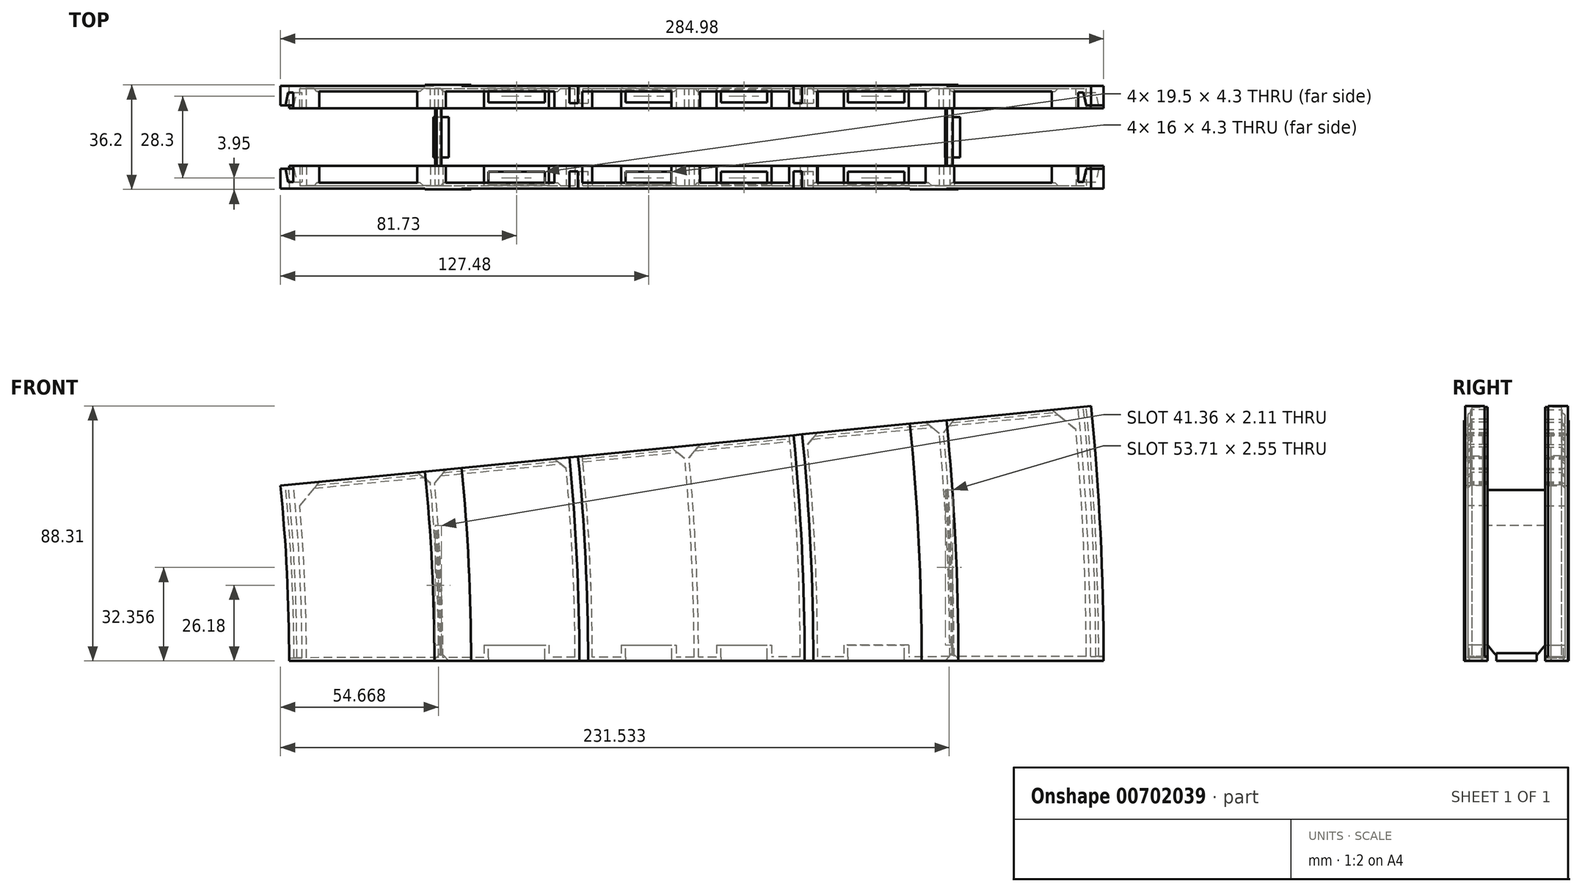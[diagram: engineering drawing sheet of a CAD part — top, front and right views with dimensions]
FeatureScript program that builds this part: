
annotation { "Feature Type Name" : "Feature", "Feature Type Description" : "" }
export const myFeature = defineFeature(function(context is Context, id is Id, definition is map)
    precondition{}
    {
        {
            var Q0;
            Q0=qCreatedBy(makeId("Top.planeOp"),FACE);
            var sketch = newSketch(context, id + "F0", { "sketchPlane" : qUnion([Q0])});
            skLineSegment(sketch, "E0", {"start": v(0, 7.8) * mm, "end": v(37.5, 7.8) * mm});
            skLineSegment(sketch, "E1", {"start": v(156, 0) * mm, "end": v(0, 0) * mm});
            skLineSegment(sketch, "E2", {"start": v(0, 0) * mm, "end": v(0, 7.8) * mm});
            skLineSegment(sketch, "E3.top", {"start": v(37.5, 1.8) * mm, "end": v(40.5, 1.8) * mm});
            skLineSegment(sketch, "E3.left", {"start": v(37.5, 7.8) * mm, "end": v(37.5, 1.8) * mm});
            skLineSegment(sketch, "E3.right", {"start": v(40.5, 7.8) * mm, "end": v(40.5, 1.8) * mm});
            skLineSegment(sketch, "E4.top", {"start": v(115.5, 1.8) * mm, "end": v(118.5, 1.8) * mm});
            skLineSegment(sketch, "E4.left", {"start": v(115.5, 7.8) * mm, "end": v(115.5, 1.8) * mm});
            skLineSegment(sketch, "E4.right", {"start": v(118.5, 7.8) * mm, "end": v(118.5, 1.8) * mm});
            skLineSegment(sketch, "E5.trimOffspring", {"start": v(40.5, 7.8) * mm, "end": v(115.5, 7.8) * mm});
            skLineSegment(sketch, "E6.trimOffspring", {"start": v(118.5, 7.8) * mm, "end": v(156, 7.8) * mm});
            skLineSegment(sketch, "E7.bottom", {"start": v(6, 6.3) * mm, "end": v(25.5, 6.3) * mm});
            skLineSegment(sketch, "E7.top", {"start": v(6, 2) * mm, "end": v(25.5, 2) * mm});
            skLineSegment(sketch, "E7.left", {"start": v(6, 6.3) * mm, "end": v(6, 2) * mm});
            skLineSegment(sketch, "E7.right", {"start": v(25.5, 6.3) * mm, "end": v(25.5, 2) * mm});
            skLineSegment(sketch, "E8.bottom", {"start": v(53.5, 6.3) * mm, "end": v(69.5, 6.3) * mm});
            skLineSegment(sketch, "E8.top", {"start": v(53.5, 2) * mm, "end": v(69.5, 2) * mm});
            skLineSegment(sketch, "E8.left", {"start": v(53.5, 6.3) * mm, "end": v(53.5, 2) * mm});
            skLineSegment(sketch, "E8.right", {"start": v(69.5, 6.3) * mm, "end": v(69.5, 2) * mm});
            skLineSegment(sketch, "E9.bottom", {"start": v(86.5, 6.3) * mm, "end": v(102.5, 6.3) * mm});
            skLineSegment(sketch, "E9.top", {"start": v(86.5, 2) * mm, "end": v(102.5, 2) * mm});
            skLineSegment(sketch, "E9.left", {"start": v(86.5, 6.3) * mm, "end": v(86.5, 2) * mm});
            skLineSegment(sketch, "E9.right", {"start": v(102.5, 6.3) * mm, "end": v(102.5, 2) * mm});
            skLineSegment(sketch, "E10.bottom", {"start": v(130.5, 6.3) * mm, "end": v(150, 6.3) * mm});
            skLineSegment(sketch, "E10.top", {"start": v(130.5, 2) * mm, "end": v(150, 2) * mm});
            skLineSegment(sketch, "E10.left", {"start": v(130.5, 6.3) * mm, "end": v(130.5, 2) * mm});
            skLineSegment(sketch, "E10.right", {"start": v(150, 6.3) * mm, "end": v(150, 2) * mm});
            skLineSegment(sketch, "E11", {"start": v(-682, 44.9) * mm, "end": v(-682, -42.13) * mm});
            skLineSegment(sketch, "E12", {"start": v(156, 7.8) * mm, "end": v(219, 7.8) * mm});
            skLineSegment(sketch, "E13", {"start": v(219, 7.8) * mm, "end": v(219, 0) * mm});
            skLineSegment(sketch, "E14", {"start": v(219, 0) * mm, "end": v(156, 0) * mm});
            skLineSegment(sketch, "E15", {"start": v(0, 0) * mm, "end": v(-63, 0) * mm});
            skLineSegment(sketch, "E16", {"start": v(-63, 0) * mm, "end": v(-63, 7.8) * mm});
            skLineSegment(sketch, "E17", {"start": v(-63, 7.8) * mm, "end": v(0, 7.8) * mm});
            skLineSegment(sketch, "E18", {"start": v(156, 7.8) * mm, "end": v(156, 0) * mm});
            skSolve(sketch);
        }
        {
            var Q0;
            Q0=makeQuery(id+"F0.imprint","IMPRINT",FACE,{"disambiguationData":[TD([[makeQuery(id+"F0.imprint","IMPRINT",EDGE,{"derivedFrom":sQuery(id+"F0.wireOp",EDGE,"E0")}),-1.0]])]});
            var Q1;
            Q1=makeQuery(id+"F0.imprint","IMPRINT",FACE,{"disambiguationData":[TD([[makeQuery(id+"F0.imprint","IMPRINT",EDGE,{"derivedFrom":sQuery(id+"F0.wireOp",EDGE,"E2")}),1.0]])]});
            var Q2;
            Q2=makeQuery(id+"F0.imprint","IMPRINT",FACE,{"disambiguationData":[TD([[makeQuery(id+"F0.imprint","IMPRINT",EDGE,{"derivedFrom":sQuery(id+"F0.wireOp",EDGE,"E12")}),-1.0]])]});
            var Q3;
            Q3=sQuery(id+"F0.wireOp",EDGE,"E11");
            revolve(context, id + "F1", {"entities" : qUnion([Q0, Q1, Q2]), "axis" : qUnion([Q3]), "revolveType" : RevolveType.ONE_DIRECTION, "angle" : .1 * degree});
        }
        {
            var Q0;
            Q0=makeQuery(id+"F1.opRevolve","CAP_FACE",FACE,{"disambiguationData":[OSD([sQuery(id+"F0.wireOp",EDGE,"E0"),sQuery(id+"F0.wireOp",EDGE,"E1"),sQuery(id+"F0.wireOp",EDGE,"E3.top"),sQuery(id+"F0.wireOp",EDGE,"E3.left"),sQuery(id+"F0.wireOp",EDGE,"E3.right"),sQuery(id+"F0.wireOp",EDGE,"E4.top"),sQuery(id+"F0.wireOp",EDGE,"E4.left"),sQuery(id+"F0.wireOp",EDGE,"E4.right"),sQuery(id+"F0.wireOp",EDGE,"E5.trimOffspring"),sQuery(id+"F0.wireOp",EDGE,"E6.trimOffspring"),sQuery(id+"F0.wireOp",EDGE,"E7.bottom"),sQuery(id+"F0.wireOp",EDGE,"E7.top"),sQuery(id+"F0.wireOp",EDGE,"E7.left"),sQuery(id+"F0.wireOp",EDGE,"E7.right"),sQuery(id+"F0.wireOp",EDGE,"E8.bottom"),sQuery(id+"F0.wireOp",EDGE,"E8.top"),sQuery(id+"F0.wireOp",EDGE,"E8.left"),sQuery(id+"F0.wireOp",EDGE,"E8.right"),sQuery(id+"F0.wireOp",EDGE,"E9.bottom"),sQuery(id+"F0.wireOp",EDGE,"E9.top"),sQuery(id+"F0.wireOp",EDGE,"E9.left"),sQuery(id+"F0.wireOp",EDGE,"E9.right"),sQuery(id+"F0.wireOp",EDGE,"E10.bottom"),sQuery(id+"F0.wireOp",EDGE,"E10.top"),sQuery(id+"F0.wireOp",EDGE,"E10.left"),sQuery(id+"F0.wireOp",EDGE,"E10.right"),sQuery(id+"F0.wireOp",EDGE,"E12"),sQuery(id+"F0.wireOp",EDGE,"E13"),sQuery(id+"F0.wireOp",EDGE,"E14"),sQuery(id+"F0.wireOp",EDGE,"E15"),sQuery(id+"F0.wireOp",EDGE,"E16"),sQuery(id+"F0.wireOp",EDGE,"E17")])],"isStart":true});
            var sketch = newSketch(context, id + "F2", { "sketchPlane" : qUnion([Q0])});
            skLineSegment(sketch, "E19", {"start": v(219, -7.8) * mm, "end": v(219, -1) * mm});
            skLineSegment(sketch, "E20", {"start": v(219, -1) * mm, "end": v(217.3, -1) * mm});
            skLineSegment(sketch, "E21", {"start": v(217.3, -1) * mm, "end": v(216.3, -5.5) * mm});
            skLineSegment(sketch, "E22", {"start": v(216.3, -5.5) * mm, "end": v(214.5, -5.5) * mm});
            skLineSegment(sketch, "E23", {"start": v(214.5, -5.5) * mm, "end": v(214.5, 0) * mm});
            skLineSegment(sketch, "E24", {"start": v(214.5, 0) * mm, "end": v(213, 0) * mm});
            skLineSegment(sketch, "E25", {"start": v(213, 0) * mm, "end": v(213, -6.8) * mm});
            skLineSegment(sketch, "E26", {"start": v(213, -6.8) * mm, "end": v(167.25, -6.8) * mm});
            skLineSegment(sketch, "E27", {"start": v(167.25, -6.8) * mm, "end": v(167.25, 0) * mm});
            skLineSegment(sketch, "E28", {"start": v(167.25, 0) * mm, "end": v(165.75, 0) * mm});
            skLineSegment(sketch, "E29", {"start": v(165.75, 0) * mm, "end": v(165.75, -6.8) * mm});
            skLineSegment(sketch, "E30", {"start": v(165.75, -6.8) * mm, "end": v(120, -6.8) * mm});
            skLineSegment(sketch, "E31", {"start": v(120, -6.8) * mm, "end": v(120, 0) * mm});
            skLineSegment(sketch, "E32", {"start": v(120, 0) * mm, "end": v(114, 0) * mm});
            skLineSegment(sketch, "E33", {"start": v(114, 0) * mm, "end": v(114, -6.8) * mm});
            skLineSegment(sketch, "E34", {"start": v(114, -6.8) * mm, "end": v(78.75, -6.8) * mm});
            skLineSegment(sketch, "E35", {"start": v(78.75, -6.8) * mm, "end": v(78.75, 0) * mm});
            skLineSegment(sketch, "E36", {"start": v(78.75, 0) * mm, "end": v(77.25, 0) * mm});
            skLineSegment(sketch, "E37", {"start": v(77.25, 0) * mm, "end": v(77.25, -6.8) * mm});
            skLineSegment(sketch, "E38", {"start": v(77.25, -6.8) * mm, "end": v(42, -6.8) * mm});
            skLineSegment(sketch, "E39", {"start": v(42, -6.8) * mm, "end": v(42, 0) * mm});
            skLineSegment(sketch, "E40", {"start": v(42, 0) * mm, "end": v(36, 0) * mm});
            skLineSegment(sketch, "E41", {"start": v(36, 0) * mm, "end": v(36, -6.8) * mm});
            skLineSegment(sketch, "E42", {"start": v(36, -6.8) * mm, "end": v(-9.75, -6.8) * mm});
            skLineSegment(sketch, "E43", {"start": v(-9.75, -6.8) * mm, "end": v(-9.75, 0) * mm});
            skLineSegment(sketch, "E44", {"start": v(-9.75, 0) * mm, "end": v(-11.25, 0) * mm});
            skLineSegment(sketch, "E45", {"start": v(-11.25, 0) * mm, "end": v(-11.25, -6.8) * mm});
            skLineSegment(sketch, "E46", {"start": v(-11.25, -6.8) * mm, "end": v(-57, -6.8) * mm});
            skLineSegment(sketch, "E47", {"start": v(-57, -6.8) * mm, "end": v(-57, 0) * mm});
            skLineSegment(sketch, "E48", {"start": v(-57, 0) * mm, "end": v(-58.5, 0) * mm});
            skLineSegment(sketch, "E49", {"start": v(-58.5, 0) * mm, "end": v(-58.5, -5.5) * mm});
            skLineSegment(sketch, "E50", {"start": v(-58.5, -5.5) * mm, "end": v(-60.3, -5.5) * mm});
            skLineSegment(sketch, "E51", {"start": v(-60.3, -5.5) * mm, "end": v(-61.3, -1) * mm});
            skLineSegment(sketch, "E52", {"start": v(-61.3, -1) * mm, "end": v(-63, -1) * mm});
            skLineSegment(sketch, "E53", {"start": v(-63, -1) * mm, "end": v(-63, -7.8) * mm});
            skLineSegment(sketch, "E54", {"start": v(-63, -7.8) * mm, "end": v(37.5, -7.8) * mm});
            skLineSegment(sketch, "E55", {"start": v(37.5, -7.8) * mm, "end": v(37.5, -1.8) * mm});
            skLineSegment(sketch, "E56", {"start": v(37.5, -1.8) * mm, "end": v(40.5, -1.8) * mm});
            skLineSegment(sketch, "E57", {"start": v(40.5, -1.8) * mm, "end": v(40.5, -7.8) * mm});
            skLineSegment(sketch, "E58", {"start": v(40.5, -7.8) * mm, "end": v(115.5, -7.8) * mm});
            skLineSegment(sketch, "E59", {"start": v(115.5, -7.8) * mm, "end": v(115.5, -1.8) * mm});
            skLineSegment(sketch, "E60", {"start": v(115.5, -1.8) * mm, "end": v(118.5, -1.8) * mm});
            skLineSegment(sketch, "E61", {"start": v(118.5, -1.8) * mm, "end": v(118.5, -7.8) * mm});
            skLineSegment(sketch, "E62", {"start": v(118.5, -7.8) * mm, "end": v(219, -7.8) * mm});
            skLineSegment(sketch, "E63", {"start": v(-682, -85.53) * mm, "end": v(-682, 67.73) * mm});
            skSolve(sketch);
        }
        {
            var Q0;
            Q0=makeQuery(id+"F2.imprint","IMPRINT",FACE,{"disambiguationData":[TD([[makeQuery(id+"F2.imprint","IMPRINT",EDGE,{"derivedFrom":sQuery(id+"F2.wireOp",EDGE,"E19")}),1.0]])]});
            var Q1;
            Q1=sQuery(id+"F2.wireOp",EDGE,"E63");
            revolve(context, id + "F3", {"operationType" : NewBodyOperationType.ADD, "entities" : qUnion([Q0]), "axis" : qUnion([Q1]), "revolveType" : RevolveType.ONE_DIRECTION, "angle" : 5.62 * degree});
        }
        {
            var Q0;
            Q0=qCreatedBy(makeId("Top.planeOp"),FACE);
            var sketch = newSketch(context, id + "F4", { "sketchPlane" : qUnion([Q0])});
            skLineSegment(sketch, "E64.bottom", {"start": v(4.5, 0) * mm, "end": v(27, 0) * mm});
            skLineSegment(sketch, "E64.top", {"start": v(4.5, 7.8) * mm, "end": v(27, 7.8) * mm});
            skLineSegment(sketch, "E64.left", {"start": v(4.5, 0) * mm, "end": v(4.5, 7.8) * mm});
            skLineSegment(sketch, "E64.right", {"start": v(27, 0) * mm, "end": v(27, 7.8) * mm});
            skLineSegment(sketch, "E65.bottom", {"start": v(6, 2) * mm, "end": v(25.5, 2) * mm});
            skLineSegment(sketch, "E65.top", {"start": v(6, 6.3) * mm, "end": v(25.5, 6.3) * mm});
            skLineSegment(sketch, "E65.left", {"start": v(6, 2) * mm, "end": v(6, 6.3) * mm});
            skLineSegment(sketch, "E65.right", {"start": v(25.5, 2) * mm, "end": v(25.5, 6.3) * mm});
            skLineSegment(sketch, "E66.bottom", {"start": v(52, 0) * mm, "end": v(71, 0) * mm});
            skLineSegment(sketch, "E66.top", {"start": v(52, 7.8) * mm, "end": v(71, 7.8) * mm});
            skLineSegment(sketch, "E66.left", {"start": v(52, 0) * mm, "end": v(52, 7.8) * mm});
            skLineSegment(sketch, "E66.right", {"start": v(71, 0) * mm, "end": v(71, 7.8) * mm});
            skLineSegment(sketch, "E67.bottom", {"start": v(53.5, 2) * mm, "end": v(69.5, 2) * mm});
            skLineSegment(sketch, "E67.top", {"start": v(53.5, 6.3) * mm, "end": v(69.5, 6.3) * mm});
            skLineSegment(sketch, "E67.left", {"start": v(53.5, 2) * mm, "end": v(53.5, 6.3) * mm});
            skLineSegment(sketch, "E67.right", {"start": v(69.5, 2) * mm, "end": v(69.5, 6.3) * mm});
            skLineSegment(sketch, "E68.bottom", {"start": v(85, 0) * mm, "end": v(104, 0) * mm});
            skLineSegment(sketch, "E68.top", {"start": v(85, 7.8) * mm, "end": v(104, 7.8) * mm});
            skLineSegment(sketch, "E68.left", {"start": v(85, 0) * mm, "end": v(85, 7.8) * mm});
            skLineSegment(sketch, "E68.right", {"start": v(104, 0) * mm, "end": v(104, 7.8) * mm});
            skLineSegment(sketch, "E69.bottom", {"start": v(86.5, 2) * mm, "end": v(102.5, 2) * mm});
            skLineSegment(sketch, "E69.top", {"start": v(86.5, 6.3) * mm, "end": v(102.5, 6.3) * mm});
            skLineSegment(sketch, "E69.left", {"start": v(86.5, 2) * mm, "end": v(86.5, 6.3) * mm});
            skLineSegment(sketch, "E69.right", {"start": v(102.5, 2) * mm, "end": v(102.5, 6.3) * mm});
            skLineSegment(sketch, "E70.top", {"start": v(129, 7.8) * mm, "end": v(151.5, 7.8) * mm});
            skLineSegment(sketch, "E70.left", {"start": v(129, 0) * mm, "end": v(129, 7.8) * mm});
            skLineSegment(sketch, "E70.right", {"start": v(151.5, 0) * mm, "end": v(151.5, 7.8) * mm});
            skLineSegment(sketch, "E71.top", {"start": v(130.5, 6.3) * mm, "end": v(150, 6.3) * mm});
            skLineSegment(sketch, "E71.left", {"start": v(130.5, 2) * mm, "end": v(130.5, 6.3) * mm});
            skLineSegment(sketch, "E71.right", {"start": v(150, 2) * mm, "end": v(150, 6.3) * mm});
            skLineSegment(sketch, "E72", {"start": v(150, 2) * mm, "end": v(130.5, 2) * mm});
            skLineSegment(sketch, "E73", {"start": v(151.5, 0) * mm, "end": v(129, 0) * mm});
            skSolve(sketch);
        }
        {
            var Q0;
            Q0=makeQuery(id+"F4.imprint","IMPRINT",FACE,{"disambiguationData":[TD([[makeQuery(id+"F4.imprint","IMPRINT",EDGE,{"derivedFrom":sQuery(id+"F4.wireOp",EDGE,"E70.top")}),-1.0]])]});
            var Q1;
            Q1=makeQuery(id+"F4.imprint","IMPRINT",FACE,{"disambiguationData":[TD([[makeQuery(id+"F4.imprint","IMPRINT",EDGE,{"derivedFrom":sQuery(id+"F4.wireOp",EDGE,"E68.bottom")}),1.0]])]});
            var Q2;
            Q2=makeQuery(id+"F4.imprint","IMPRINT",FACE,{"disambiguationData":[TD([[makeQuery(id+"F4.imprint","IMPRINT",EDGE,{"derivedFrom":sQuery(id+"F4.wireOp",EDGE,"E66.bottom")}),1.0]])]});
            var Q3;
            Q3=makeQuery(id+"F4.imprint","IMPRINT",FACE,{"disambiguationData":[TD([[makeQuery(id+"F4.imprint","IMPRINT",EDGE,{"derivedFrom":sQuery(id+"F4.wireOp",EDGE,"E64.bottom")}),1.0]])]});
            extrude(context, id + "F5", {"entities" : qUnion([Q0, Q1, Q2, Q3]), "operationType" : NewBodyOperationType.ADD, "depth" : 5.5 * mm, "offsetDistance" : 25 * mm});
        }
        {
            var Q0;
            Q0=makeQuery(id+"FsCbM9j6MyeHqur_1.boolean.opBoolean","MERGE",FACE,{"derivedFrom":[makeQuery(id+"F3.opRevolve","CAP_FACE",FACE,{"disambiguationData":[OSD([sQuery(id+"F2.wireOp",EDGE,"E19"),sQuery(id+"F2.wireOp",EDGE,"E20"),sQuery(id+"F2.wireOp",EDGE,"E21"),sQuery(id+"F2.wireOp",EDGE,"E22"),sQuery(id+"F2.wireOp",EDGE,"E23"),sQuery(id+"F2.wireOp",EDGE,"E24"),sQuery(id+"F2.wireOp",EDGE,"E25"),sQuery(id+"F2.wireOp",EDGE,"E26"),sQuery(id+"F2.wireOp",EDGE,"E27"),sQuery(id+"F2.wireOp",EDGE,"E28"),sQuery(id+"F2.wireOp",EDGE,"E29"),sQuery(id+"F2.wireOp",EDGE,"E30"),sQuery(id+"F2.wireOp",EDGE,"E31"),sQuery(id+"F2.wireOp",EDGE,"E32"),sQuery(id+"F2.wireOp",EDGE,"E33"),sQuery(id+"F2.wireOp",EDGE,"E34"),sQuery(id+"F2.wireOp",EDGE,"E35"),sQuery(id+"F2.wireOp",EDGE,"E36"),sQuery(id+"F2.wireOp",EDGE,"E37"),sQuery(id+"F2.wireOp",EDGE,"E38"),sQuery(id+"F2.wireOp",EDGE,"E39"),sQuery(id+"F2.wireOp",EDGE,"E40"),sQuery(id+"F2.wireOp",EDGE,"E41"),sQuery(id+"F2.wireOp",EDGE,"E42"),sQuery(id+"F2.wireOp",EDGE,"E43"),sQuery(id+"F2.wireOp",EDGE,"E44"),sQuery(id+"F2.wireOp",EDGE,"E45"),sQuery(id+"F2.wireOp",EDGE,"E46"),sQuery(id+"F2.wireOp",EDGE,"E47"),sQuery(id+"F2.wireOp",EDGE,"E48"),sQuery(id+"F2.wireOp",EDGE,"E49"),sQuery(id+"F2.wireOp",EDGE,"E50"),sQuery(id+"F2.wireOp",EDGE,"E51"),sQuery(id+"F2.wireOp",EDGE,"E52"),sQuery(id+"F2.wireOp",EDGE,"E53"),sQuery(id+"F2.wireOp",EDGE,"E54"),sQuery(id+"F2.wireOp",EDGE,"E55"),sQuery(id+"F2.wireOp",EDGE,"E56"),sQuery(id+"F2.wireOp",EDGE,"E57"),sQuery(id+"F2.wireOp",EDGE,"E58"),sQuery(id+"F2.wireOp",EDGE,"E59"),sQuery(id+"F2.wireOp",EDGE,"E60"),sQuery(id+"F2.wireOp",EDGE,"E61"),sQuery(id+"F2.wireOp",EDGE,"E62")])],"isStart":false}),makeQuery(id+"FsCbM9j6MyeHqur_1.opRevolve","CAP_FACE",FACE,{"disambiguationData":[OSD([sQuery(id+"FyRx6zC8CaxFU6Y_1.wireOp",EDGE,"8ZVv8dg5-GuJE-Izcm-uAng-MruvJyQP3tpH.bottom"),sQuery(id+"FyRx6zC8CaxFU6Y_1.wireOp",EDGE,"8ZVv8dg5-GuJE-Izcm-uAng-MruvJyQP3tpH.top"),sQuery(id+"FyRx6zC8CaxFU6Y_1.wireOp",EDGE,"8ZVv8dg5-GuJE-Izcm-uAng-MruvJyQP3tpH.left"),sQuery(id+"FyRx6zC8CaxFU6Y_1.wireOp",EDGE,"8ZVv8dg5-GuJE-Izcm-uAng-MruvJyQP3tpH.right")])],"isStart":false}),makeQuery(id+"FsCbM9j6MyeHqur_1.opRevolve","CAP_FACE",FACE,{"disambiguationData":[OSD([sQuery(id+"FyRx6zC8CaxFU6Y_1.wireOp",EDGE,"LG1o2c2C-Ix52-DPfE-WXm3-svmOJ2u8Z8Do.bottom"),sQuery(id+"FyRx6zC8CaxFU6Y_1.wireOp",EDGE,"LG1o2c2C-Ix52-DPfE-WXm3-svmOJ2u8Z8Do.top"),sQuery(id+"FyRx6zC8CaxFU6Y_1.wireOp",EDGE,"LG1o2c2C-Ix52-DPfE-WXm3-svmOJ2u8Z8Do.left"),sQuery(id+"FyRx6zC8CaxFU6Y_1.wireOp",EDGE,"LG1o2c2C-Ix52-DPfE-WXm3-svmOJ2u8Z8Do.right")])],"isStart":false})]});
            var sketch = newSketch(context, id + "F6", { "sketchPlane" : qUnion([Q0])});
            skLineSegment(sketch, "E74.bottom", {"start": v(-54.5, 7.8) * mm, "end": v(226.06, 7.8) * mm});
            skLineSegment(sketch, "E74.top", {"start": v(-54.5, 5.8) * mm, "end": v(226.06, 5.8) * mm});
            skLineSegment(sketch, "E74.left", {"start": v(-54.5, 7.8) * mm, "end": v(-54.5, 5.8) * mm});
            skLineSegment(sketch, "E74.right", {"start": v(226.06, 7.8) * mm, "end": v(226.06, 5.8) * mm});
            skSolve(sketch);
        }
        {
            var Q0;
            {var subQ5=makeQuery(id+"F3.opRevolve","CAP_EDGE",EDGE,{"disambiguationData":[OSD([sQuery(id+"F2.wireOp",EDGE,"E46")])],"isStart":false});Q0=makeQuery(id+"F6.imprint","IMPRINT",FACE,{"disambiguationData":[TD([[makeQuery(id+"F6.imprint","IMPRINT",EDGE,{"derivedFrom":subQ5}),1.0]])]});}
            var Q1;
            {var subQ0=sQuery(id+"F6.wireOp",EDGE,"E74.left");Q1=makeQuery(id+"F6.imprint","IMPRINT",FACE,{"disambiguationData":[TD([[makeQuery(id+"F6.imprint","IMPRINT",EDGE,{"derivedFrom":subQ0}),1.0]])]});}
            var Q2;
            {var subQ5=makeQuery(id+"F3.opRevolve","CAP_EDGE",EDGE,{"disambiguationData":[OSD([sQuery(id+"F2.wireOp",EDGE,"E42")])],"isStart":false});Q2=makeQuery(id+"F6.imprint","IMPRINT",FACE,{"disambiguationData":[TD([[makeQuery(id+"F6.imprint","IMPRINT",EDGE,{"derivedFrom":subQ5}),1.0]])]});}
            var Q3;
            {var subQ7=makeQuery(id+"F3.opRevolve","CAP_EDGE",EDGE,{"disambiguationData":[OSD([sQuery(id+"F2.wireOp",EDGE,"E34")])],"isStart":false});Q3=makeQuery(id+"F6.imprint","IMPRINT",FACE,{"disambiguationData":[TD([[makeQuery(id+"F6.imprint","IMPRINT",EDGE,{"derivedFrom":subQ7}),-1.0]])]});}
            var Q4;
            {var subQ5=makeQuery(id+"F3.opRevolve","CAP_EDGE",EDGE,{"disambiguationData":[OSD([sQuery(id+"F2.wireOp",EDGE,"E38")])],"isStart":false});Q4=makeQuery(id+"F6.imprint","IMPRINT",FACE,{"disambiguationData":[TD([[makeQuery(id+"F6.imprint","IMPRINT",EDGE,{"derivedFrom":subQ5}),1.0]])]});}
            var Q5;
            {var subQ5=makeQuery(id+"F3.opRevolve","CAP_EDGE",EDGE,{"disambiguationData":[OSD([sQuery(id+"F2.wireOp",EDGE,"E34")])],"isStart":false});Q5=makeQuery(id+"F6.imprint","IMPRINT",FACE,{"disambiguationData":[TD([[makeQuery(id+"F6.imprint","IMPRINT",EDGE,{"derivedFrom":subQ5}),1.0]])]});}
            var Q6;
            {var subQ0=makeQuery(id+"F3.opRevolve","CAP_EDGE",EDGE,{"disambiguationData":[OSD([sQuery(id+"F2.wireOp",EDGE,"E26")])],"isStart":false});Q6=makeQuery(id+"F6.imprint","IMPRINT",FACE,{"disambiguationData":[TD([[makeQuery(id+"F6.imprint","IMPRINT",EDGE,{"derivedFrom":subQ0}),-1.0]])]});}
            var Q7;
            {var subQ5=makeQuery(id+"F3.opRevolve","CAP_EDGE",EDGE,{"disambiguationData":[OSD([sQuery(id+"F2.wireOp",EDGE,"E30")])],"isStart":false});Q7=makeQuery(id+"F6.imprint","IMPRINT",FACE,{"disambiguationData":[TD([[makeQuery(id+"F6.imprint","IMPRINT",EDGE,{"derivedFrom":subQ5}),1.0]])]});}
            var Q8;
            {var subQ5=makeQuery(id+"F3.opRevolve","CAP_EDGE",EDGE,{"disambiguationData":[OSD([sQuery(id+"F2.wireOp",EDGE,"E26")])],"isStart":false});Q8=makeQuery(id+"F6.imprint","IMPRINT",FACE,{"disambiguationData":[TD([[makeQuery(id+"F6.imprint","IMPRINT",EDGE,{"derivedFrom":subQ5}),1.0]])]});}
            var Q9;
            {var subQ3=sQuery(id+"F6.wireOp",EDGE,"E74.right");Q9=makeQuery(id+"F6.imprint","IMPRINT",FACE,{"disambiguationData":[TD([[makeQuery(id+"F6.imprint","IMPRINT",EDGE,{"derivedFrom":subQ3}),-1.0]])]});}
            var Q10;
            {var subQ0=sQuery(id+"F6.wireOp",EDGE,"E74.bottom");var subQ1=makeQuery(id+"F3.opRevolve","CAP_EDGE",EDGE,{"disambiguationData":[OSD([sQuery(id+"F2.wireOp",EDGE,"E59")])],"isStart":false});var subQ2=makeQuery(id+"F6.imprint","INTERSECT",VERTEX,{"derivedFrom":[subQ1,subQ0]});Q10=makeQuery(id+"F6.imprint","IMPRINT",FACE,{"disambiguationData":[TD([[makeQuery(id+"F6.imprint","IMPRINT",EDGE,{"disambiguationData":[TD([[subQ2,-1.0]])],"derivedFrom":subQ0}),-1.0]])]});}
            var Q11;
            {var subQ0=sQuery(id+"F6.wireOp",EDGE,"E74.bottom");var subQ1=makeQuery(id+"F3.opRevolve","CAP_EDGE",EDGE,{"disambiguationData":[OSD([sQuery(id+"F2.wireOp",EDGE,"E55")])],"isStart":false});var subQ2=makeQuery(id+"F6.imprint","INTERSECT",VERTEX,{"derivedFrom":[subQ1,subQ0]});Q11=makeQuery(id+"F6.imprint","IMPRINT",FACE,{"disambiguationData":[TD([[makeQuery(id+"F6.imprint","IMPRINT",EDGE,{"disambiguationData":[TD([[subQ2,-1.0]])],"derivedFrom":subQ0}),-1.0]])]});}
            extrude(context, id + "F7", {"entities" : qUnion([Q0, Q1, Q2, Q3, Q4, Q5, Q6, Q7, Q8, Q9, Q10, Q11]), "operationType" : NewBodyOperationType.ADD, "oppositeDirection" : true, "depth" : 1 * mm, "offsetDistance" : 25 * mm});
        }
        {
            var Q0;
            Q0=makeQuery(id+"F7.opExtrude","SWEPT_FACE",FACE,{"disambiguationData":[OSD([sQuery(id+"F6.wireOp",EDGE,"E74.right")])]});
            var sketch = newSketch(context, id + "F8", { "sketchPlane" : qUnion([Q0])});
            skLineSegment(sketch, "E75", {"start": v(5.8, 66.85) * mm, "end": v(5.8, 65.85) * mm});
            skLineSegment(sketch, "E76", {"start": v(5.8, 65.85) * mm, "end": v(7.04, 64.6) * mm});
            skLineSegment(sketch, "E77", {"start": v(7.04, 64.6) * mm, "end": v(7.04, 66.85) * mm});
            skLineSegment(sketch, "E78", {"start": v(7.04, 66.85) * mm, "end": v(5.8, 66.85) * mm});
            skSolve(sketch);
        }
        {
            var Q0;
            {var subQ0=sQuery(id+"F8.wireOp",EDGE,"E75");Q0=makeQuery(id+"F8.imprint","IMPRINT",FACE,{"disambiguationData":[TD([[makeQuery(id+"F8.imprint","IMPRINT",EDGE,{"derivedFrom":subQ0}),-1.0]])]});}
            var Q1;
            {var subQ0=sQuery(id+"F8.wireOp",EDGE,"E76");Q1=makeQuery(id+"F8.imprint","IMPRINT",FACE,{"disambiguationData":[TD([[makeQuery(id+"F8.imprint","IMPRINT",EDGE,{"derivedFrom":subQ0}),1.0]])]});}
            extrude(context, id + "F9", {"entities" : qUnion([Q0, Q1]), "operationType" : NewBodyOperationType.ADD, "oppositeDirection" : true, "depth" : 282.16 * mm, "offsetDistance" : 25 * mm});
        }
        {
            var Q0;
            Q0=makeQuery(id+"FsCbM9j6MyeHqur_1.boolean.opBoolean","MERGE",FACE,{"derivedFrom":[makeQuery(id+"F1.opRevolve","CAP_FACE",FACE,{"disambiguationData":[OSD([sQuery(id+"F0.wireOp",EDGE,"E0"),sQuery(id+"F0.wireOp",EDGE,"E1"),sQuery(id+"F0.wireOp",EDGE,"E3.top"),sQuery(id+"F0.wireOp",EDGE,"E3.left"),sQuery(id+"F0.wireOp",EDGE,"E3.right"),sQuery(id+"F0.wireOp",EDGE,"E4.top"),sQuery(id+"F0.wireOp",EDGE,"E4.left"),sQuery(id+"F0.wireOp",EDGE,"E4.right"),sQuery(id+"F0.wireOp",EDGE,"E5.trimOffspring"),sQuery(id+"F0.wireOp",EDGE,"E6.trimOffspring"),sQuery(id+"F0.wireOp",EDGE,"E7.bottom"),sQuery(id+"F0.wireOp",EDGE,"E7.top"),sQuery(id+"F0.wireOp",EDGE,"E7.left"),sQuery(id+"F0.wireOp",EDGE,"E7.right"),sQuery(id+"F0.wireOp",EDGE,"E8.bottom"),sQuery(id+"F0.wireOp",EDGE,"E8.top"),sQuery(id+"F0.wireOp",EDGE,"E8.left"),sQuery(id+"F0.wireOp",EDGE,"E8.right"),sQuery(id+"F0.wireOp",EDGE,"E9.bottom"),sQuery(id+"F0.wireOp",EDGE,"E9.top"),sQuery(id+"F0.wireOp",EDGE,"E9.left"),sQuery(id+"F0.wireOp",EDGE,"E9.right"),sQuery(id+"F0.wireOp",EDGE,"E10.bottom"),sQuery(id+"F0.wireOp",EDGE,"E10.top"),sQuery(id+"F0.wireOp",EDGE,"E10.left"),sQuery(id+"F0.wireOp",EDGE,"E10.right"),sQuery(id+"F0.wireOp",EDGE,"E12"),sQuery(id+"F0.wireOp",EDGE,"E13"),sQuery(id+"F0.wireOp",EDGE,"E14"),sQuery(id+"F0.wireOp",EDGE,"E15"),sQuery(id+"F0.wireOp",EDGE,"E16"),sQuery(id+"F0.wireOp",EDGE,"E17")])],"isStart":true}),makeQuery(id+"FsCbM9j6MyeHqur_1.opRevolve","CAP_FACE",FACE,{"disambiguationData":[OSD([sQuery(id+"FyRx6zC8CaxFU6Y_1.wireOp",EDGE,"8ZVv8dg5-GuJE-Izcm-uAng-MruvJyQP3tpH.bottom"),sQuery(id+"FyRx6zC8CaxFU6Y_1.wireOp",EDGE,"8ZVv8dg5-GuJE-Izcm-uAng-MruvJyQP3tpH.top"),sQuery(id+"FyRx6zC8CaxFU6Y_1.wireOp",EDGE,"8ZVv8dg5-GuJE-Izcm-uAng-MruvJyQP3tpH.left"),sQuery(id+"FyRx6zC8CaxFU6Y_1.wireOp",EDGE,"8ZVv8dg5-GuJE-Izcm-uAng-MruvJyQP3tpH.right")])],"isStart":true}),makeQuery(id+"FsCbM9j6MyeHqur_1.opRevolve","CAP_FACE",FACE,{"disambiguationData":[OSD([sQuery(id+"FyRx6zC8CaxFU6Y_1.wireOp",EDGE,"LG1o2c2C-Ix52-DPfE-WXm3-svmOJ2u8Z8Do.bottom"),sQuery(id+"FyRx6zC8CaxFU6Y_1.wireOp",EDGE,"LG1o2c2C-Ix52-DPfE-WXm3-svmOJ2u8Z8Do.top"),sQuery(id+"FyRx6zC8CaxFU6Y_1.wireOp",EDGE,"LG1o2c2C-Ix52-DPfE-WXm3-svmOJ2u8Z8Do.left"),sQuery(id+"FyRx6zC8CaxFU6Y_1.wireOp",EDGE,"LG1o2c2C-Ix52-DPfE-WXm3-svmOJ2u8Z8Do.right")])],"isStart":true})]});
            var sketch = newSketch(context, id + "F10", { "sketchPlane" : qUnion([Q0])});
            skLineSegment(sketch, "E79.bottom", {"start": v(118.5, -1.8) * mm, "end": v(115.5, -1.8) * mm});
            skLineSegment(sketch, "E79.top", {"start": v(118.5, -11.8) * mm, "end": v(115.5, -11.8) * mm});
            skLineSegment(sketch, "E79.left", {"start": v(118.5, -1.8) * mm, "end": v(118.5, -11.8) * mm});
            skLineSegment(sketch, "E79.right", {"start": v(115.5, -1.8) * mm, "end": v(115.5, -11.8) * mm});
            skLineSegment(sketch, "E80.bottom", {"start": v(40.5, -1.8) * mm, "end": v(37.5, -1.8) * mm});
            skLineSegment(sketch, "E80.top", {"start": v(40.5, -12.99) * mm, "end": v(37.5, -12.99) * mm});
            skLineSegment(sketch, "E80.left", {"start": v(40.5, -1.8) * mm, "end": v(40.5, -12.99) * mm});
            skLineSegment(sketch, "E80.right", {"start": v(37.5, -1.8) * mm, "end": v(37.5, -12.99) * mm});
            skLineSegment(sketch, "E81.bottom", {"start": v(219, 0) * mm, "end": v(229.37, 0) * mm});
            skLineSegment(sketch, "E81.top", {"start": v(219, -12.92) * mm, "end": v(229.37, -12.92) * mm});
            skLineSegment(sketch, "E81.left", {"start": v(219, 0) * mm, "end": v(219, -12.92) * mm});
            skLineSegment(sketch, "E81.right", {"start": v(229.37, 0) * mm, "end": v(229.37, -12.92) * mm});
            skLineSegment(sketch, "E82", {"start": v(-682, -71.97) * mm, "end": v(-682, 175.77) * mm});
            skSolve(sketch);
        }
        {
            var Q0;
            {var subQ10=sQuery(id+"F10.wireOp",EDGE,"E81.bottom");Q0=makeQuery(id+"F10.imprint","IMPRINT",FACE,{"disambiguationData":[TD([[makeQuery(id+"F10.imprint","IMPRINT",EDGE,{"derivedFrom":subQ10}),-1.0]])]});}
            var Q1;
            {var subQ8=sQuery(id+"F10.wireOp",EDGE,"E79.bottom");Q1=makeQuery(id+"F10.imprint","IMPRINT",FACE,{"disambiguationData":[TD([[makeQuery(id+"F10.imprint","IMPRINT",EDGE,{"derivedFrom":subQ8}),-1.0]])]});}
            var Q2;
            {var subQ4=sQuery(id+"F10.wireOp",EDGE,"E80.bottom");Q2=makeQuery(id+"F10.imprint","IMPRINT",FACE,{"disambiguationData":[TD([[makeQuery(id+"F10.imprint","IMPRINT",EDGE,{"derivedFrom":subQ4}),-1.0]])]});}
            var Q3;
            Q3=sQuery(id+"F10.wireOp",EDGE,"E82");
            revolve(context, id + "F11", {"operationType" : NewBodyOperationType.REMOVE, "entities" : qUnion([Q0, Q1, Q2]), "axis" : qUnion([Q3]), "revolveType" : RevolveType.FULL, "oppositeDirection" : true});
        }
        {
            var Q0;
            {var subQ1=sQuery(id+"F2.wireOp",EDGE,"E62");var subQ2=sQuery(id+"F2.wireOp",EDGE,"E58");var subQ4=sQuery(id+"F2.wireOp",EDGE,"E54");var subQ6=sQuery(id+"F0.wireOp",EDGE,"E3.left");var subQ7=sQuery(id+"F0.wireOp",EDGE,"E17");var subQ8=sQuery(id+"F0.wireOp",EDGE,"E12");var subQ9=sQuery(id+"F0.wireOp",EDGE,"E6.trimOffspring");var subQ10=sQuery(id+"F0.wireOp",EDGE,"E5.trimOffspring");var subQ11=sQuery(id+"F0.wireOp",EDGE,"E0");var subQ12=sQuery(id+"F6.wireOp",EDGE,"E74.bottom");Q0=makeQuery(id+"F11.boolean.opBoolean","SPLIT",FACE,{"disambiguationData":[TD([makeQuery(id+"F1.opRevolve","SWEPT_FACE",FACE,{"disambiguationData":[OSD([subQ6])]})])],"derivedFrom":makeQuery(id+"F7.boolean.opBoolean","MERGE",FACE,{"derivedFrom":[makeQuery(id+"F3.boolean.opBoolean","MERGE",FACE,{"derivedFrom":[makeQuery(id+"F1.opRevolve","SWEPT_FACE",FACE,{"disambiguationData":[OSD([subQ11,subQ7])]}),makeQuery(id+"F3.opRevolve","SWEPT_FACE",FACE,{"disambiguationData":[OSD([subQ4])]})]}),makeQuery(id+"F3.boolean.opBoolean","MERGE",FACE,{"derivedFrom":[makeQuery(id+"F1.opRevolve","SWEPT_FACE",FACE,{"disambiguationData":[OSD([subQ10])]}),makeQuery(id+"F3.opRevolve","SWEPT_FACE",FACE,{"disambiguationData":[OSD([subQ2])]})]}),makeQuery(id+"F3.boolean.opBoolean","MERGE",FACE,{"derivedFrom":[makeQuery(id+"F1.opRevolve","SWEPT_FACE",FACE,{"disambiguationData":[OSD([subQ9,subQ8])]}),makeQuery(id+"F3.opRevolve","SWEPT_FACE",FACE,{"disambiguationData":[OSD([subQ1])]})]}),makeQuery(id+"F7.opExtrude","SWEPT_FACE",FACE,{"disambiguationData":[OSD([subQ12])]})]})});}
            var sketch = newSketch(context, id + "F12", { "sketchPlane" : qUnion([Q0])});
            skLineSegment(sketch, "E83", {"start": v(-32.85, 70.4) * mm, "end": v(-33.24, 66.43) * mm});
            skLineSegment(sketch, "E84", {"start": v(-33.24, 66.43) * mm, "end": v(-28.87, 70.01) * mm});
            skLineSegment(sketch, "E85", {"start": v(-28.87, 70.01) * mm, "end": v(-32.85, 70.4) * mm});
            skLineSegment(sketch, "E86", {"start": v(60.45, 61.22) * mm, "end": v(59.67, 53.26) * mm});
            skLineSegment(sketch, "E87", {"start": v(59.67, 53.26) * mm, "end": v(52.49, 62) * mm});
            skLineSegment(sketch, "E88", {"start": v(52.49, 62) * mm, "end": v(60.45, 61.22) * mm});
            skLineSegment(sketch, "E89", {"start": v(18.66, 65.33) * mm, "end": v(13.2, 60.85) * mm});
            skLineSegment(sketch, "E90", {"start": v(13.2, 60.85) * mm, "end": v(8.71, 66.31) * mm});
            skLineSegment(sketch, "E91", {"start": v(8.71, 66.31) * mm, "end": v(18.66, 65.33) * mm});
            skSolve(sketch);
        }
        {
            var Q0;
            Q0=makeQuery(id+"F12.imprint","IMPRINT",FACE,{"disambiguationData":[TD([[makeQuery(id+"F12.imprint","IMPRINT",EDGE,{"derivedFrom":sQuery(id+"F12.wireOp",EDGE,"E89")}),-1.0]])]});
            var Q1;
            Q1=makeQuery(id+"F12.imprint","IMPRINT",FACE,{"disambiguationData":[TD([[makeQuery(id+"F12.imprint","IMPRINT",EDGE,{"derivedFrom":sQuery(id+"F12.wireOp",EDGE,"E83")}),1.0]])]});
            var Q2;
            Q2=makeQuery(id+"F12.imprint","IMPRINT",FACE,{"disambiguationData":[TD([[makeQuery(id+"F12.imprint","IMPRINT",EDGE,{"derivedFrom":sQuery(id+"F12.wireOp",EDGE,"E86")}),-1.0]])]});
            extrude(context, id + "F13", {"entities" : qUnion([Q0, Q1, Q2]), "operationType" : NewBodyOperationType.ADD, "oppositeDirection" : true, "depth" : 7.8 * mm, "offsetDistance" : 25 * mm});
        }
        {
            var Q0;
            {var subQ2=sQuery(id+"F6.wireOp",EDGE,"E74.bottom");var subQ4=sQuery(id+"F0.wireOp",EDGE,"E4.right");var subQ5=sQuery(id+"F0.wireOp",EDGE,"E17");var subQ6=sQuery(id+"F0.wireOp",EDGE,"E12");var subQ7=sQuery(id+"F0.wireOp",EDGE,"E6.trimOffspring");var subQ8=sQuery(id+"F0.wireOp",EDGE,"E5.trimOffspring");var subQ9=sQuery(id+"F0.wireOp",EDGE,"E0");var subQ10=sQuery(id+"F2.wireOp",EDGE,"E62");var subQ11=sQuery(id+"F2.wireOp",EDGE,"E58");var subQ12=sQuery(id+"F2.wireOp",EDGE,"E54");Q0=makeQuery(id+"F11.boolean.opBoolean","SPLIT",FACE,{"disambiguationData":[TD([makeQuery(id+"F1.opRevolve","SWEPT_FACE",FACE,{"disambiguationData":[OSD([subQ4])]})])],"derivedFrom":makeQuery(id+"F7.boolean.opBoolean","MERGE",FACE,{"derivedFrom":[makeQuery(id+"F3.boolean.opBoolean","MERGE",FACE,{"derivedFrom":[makeQuery(id+"F1.opRevolve","SWEPT_FACE",FACE,{"disambiguationData":[OSD([subQ9,subQ5])]}),makeQuery(id+"F3.opRevolve","SWEPT_FACE",FACE,{"disambiguationData":[OSD([subQ12])]})]}),makeQuery(id+"F3.boolean.opBoolean","MERGE",FACE,{"derivedFrom":[makeQuery(id+"F1.opRevolve","SWEPT_FACE",FACE,{"disambiguationData":[OSD([subQ8])]}),makeQuery(id+"F3.opRevolve","SWEPT_FACE",FACE,{"disambiguationData":[OSD([subQ11])]})]}),makeQuery(id+"F3.boolean.opBoolean","MERGE",FACE,{"derivedFrom":[makeQuery(id+"F1.opRevolve","SWEPT_FACE",FACE,{"disambiguationData":[OSD([subQ7,subQ6])]}),makeQuery(id+"F3.opRevolve","SWEPT_FACE",FACE,{"disambiguationData":[OSD([subQ10])]})]}),makeQuery(id+"F7.opExtrude","SWEPT_FACE",FACE,{"disambiguationData":[OSD([subQ2])]})]})});}
            var sketch = newSketch(context, id + "F14", { "sketchPlane" : qUnion([Q0])});
            skLineSegment(sketch, "E92", {"start": v(-209.03, 87.76) * mm, "end": v(-209.82, 79.8) * mm});
            skLineSegment(sketch, "E93", {"start": v(-209.82, 79.8) * mm, "end": v(-201.07, 86.98) * mm});
            skLineSegment(sketch, "E94", {"start": v(-201.07, 86.98) * mm, "end": v(-209.03, 87.76) * mm});
            skLineSegment(sketch, "E95", {"start": v(-167.32, 83.65) * mm, "end": v(-157.36, 82.67) * mm});
            skLineSegment(sketch, "E96", {"start": v(-157.36, 82.67) * mm, "end": v(-162.83, 78.18) * mm});
            skLineSegment(sketch, "E97", {"start": v(-162.83, 78.18) * mm, "end": v(-167.32, 83.65) * mm});
            skLineSegment(sketch, "E98", {"start": v(-119.8, 78.97) * mm, "end": v(-115.81, 78.58) * mm});
            skLineSegment(sketch, "E99", {"start": v(-115.81, 78.58) * mm, "end": v(-116.2, 74.6) * mm});
            skLineSegment(sketch, "E100", {"start": v(-116.2, 74.6) * mm, "end": v(-119.8, 78.97) * mm});
            skSolve(sketch);
        }
        {
            var Q0;
            Q0=makeQuery(id+"F14.imprint","IMPRINT",FACE,{"disambiguationData":[TD([[makeQuery(id+"F14.imprint","IMPRINT",EDGE,{"derivedFrom":sQuery(id+"F14.wireOp",EDGE,"E92")}),1.0]])]});
            var Q1;
            Q1=makeQuery(id+"F14.imprint","IMPRINT",FACE,{"disambiguationData":[TD([[makeQuery(id+"F14.imprint","IMPRINT",EDGE,{"derivedFrom":sQuery(id+"F14.wireOp",EDGE,"E95")}),1.0]])]});
            var Q2;
            Q2=makeQuery(id+"F14.imprint","IMPRINT",FACE,{"disambiguationData":[TD([[makeQuery(id+"F14.imprint","IMPRINT",EDGE,{"derivedFrom":sQuery(id+"F14.wireOp",EDGE,"E98")}),1.0]])]});
            extrude(context, id + "F15", {"entities" : qUnion([Q0, Q1, Q2]), "operationType" : NewBodyOperationType.ADD, "oppositeDirection" : true, "depth" : 7.8 * mm, "offsetDistance" : 25 * mm});
        }
        {
            var Q0;
            {var subQ2=sQuery(id+"F0.wireOp",EDGE,"E3.right");var subQ3=sQuery(id+"F2.wireOp",EDGE,"E62");var subQ5=sQuery(id+"F2.wireOp",EDGE,"E58");var subQ6=sQuery(id+"F2.wireOp",EDGE,"E54");var subQ7=sQuery(id+"F0.wireOp",EDGE,"E17");var subQ8=sQuery(id+"F0.wireOp",EDGE,"E12");var subQ9=sQuery(id+"F0.wireOp",EDGE,"E6.trimOffspring");var subQ10=sQuery(id+"F0.wireOp",EDGE,"E5.trimOffspring");var subQ11=sQuery(id+"F0.wireOp",EDGE,"E0");var subQ12=sQuery(id+"F6.wireOp",EDGE,"E74.bottom");Q0=makeQuery(id+"F11.boolean.opBoolean","SPLIT",FACE,{"disambiguationData":[TD([makeQuery(id+"F1.opRevolve","SWEPT_FACE",FACE,{"disambiguationData":[OSD([subQ2])]})])],"derivedFrom":makeQuery(id+"F7.boolean.opBoolean","MERGE",FACE,{"derivedFrom":[makeQuery(id+"F3.boolean.opBoolean","MERGE",FACE,{"derivedFrom":[makeQuery(id+"F1.opRevolve","SWEPT_FACE",FACE,{"disambiguationData":[OSD([subQ11,subQ7])]}),makeQuery(id+"F3.opRevolve","SWEPT_FACE",FACE,{"disambiguationData":[OSD([subQ6])]})]}),makeQuery(id+"F3.boolean.opBoolean","MERGE",FACE,{"derivedFrom":[makeQuery(id+"F1.opRevolve","SWEPT_FACE",FACE,{"disambiguationData":[OSD([subQ10])]}),makeQuery(id+"F3.opRevolve","SWEPT_FACE",FACE,{"disambiguationData":[OSD([subQ5])]})]}),makeQuery(id+"F3.boolean.opBoolean","MERGE",FACE,{"derivedFrom":[makeQuery(id+"F1.opRevolve","SWEPT_FACE",FACE,{"disambiguationData":[OSD([subQ9,subQ8])]}),makeQuery(id+"F3.opRevolve","SWEPT_FACE",FACE,{"disambiguationData":[OSD([subQ3])]})]}),makeQuery(id+"F7.opExtrude","SWEPT_FACE",FACE,{"disambiguationData":[OSD([subQ12])]})]})});}
            var sketch = newSketch(context, id + "F16", { "sketchPlane" : qUnion([Q0])});
            skLineSegment(sketch, "E101", {"start": v(-69.33, 74) * mm, "end": v(-79.28, 74.98) * mm});
            skLineSegment(sketch, "E102", {"start": v(-79.28, 74.98) * mm, "end": v(-74.8, 69.51) * mm});
            skLineSegment(sketch, "E103", {"start": v(-74.8, 69.51) * mm, "end": v(-69.33, 74) * mm});
            skSolve(sketch);
        }
        {
            var Q0;
            Q0=makeQuery(id+"F16.imprint","IMPRINT",FACE,{"disambiguationData":[TD([[makeQuery(id+"F16.imprint","IMPRINT",EDGE,{"derivedFrom":sQuery(id+"F16.wireOp",EDGE,"E101")}),1.0]])]});
            extrude(context, id + "F17", {"entities" : qUnion([Q0]), "operationType" : NewBodyOperationType.ADD, "oppositeDirection" : true, "depth" : 7.8 * mm, "offsetDistance" : 25 * mm});
        }
        {
            var Q0;
            Q0=makeQuery(id+"F1.opRevolve","CAP_FACE",FACE,{"disambiguationData":[OSD([sQuery(id+"F0.wireOp",EDGE,"E0"),sQuery(id+"F0.wireOp",EDGE,"E1"),sQuery(id+"F0.wireOp",EDGE,"E3.top"),sQuery(id+"F0.wireOp",EDGE,"E3.left"),sQuery(id+"F0.wireOp",EDGE,"E3.right"),sQuery(id+"F0.wireOp",EDGE,"E4.top"),sQuery(id+"F0.wireOp",EDGE,"E4.left"),sQuery(id+"F0.wireOp",EDGE,"E4.right"),sQuery(id+"F0.wireOp",EDGE,"E5.trimOffspring"),sQuery(id+"F0.wireOp",EDGE,"E6.trimOffspring"),sQuery(id+"F0.wireOp",EDGE,"E7.bottom"),sQuery(id+"F0.wireOp",EDGE,"E7.top"),sQuery(id+"F0.wireOp",EDGE,"E7.left"),sQuery(id+"F0.wireOp",EDGE,"E7.right"),sQuery(id+"F0.wireOp",EDGE,"E8.bottom"),sQuery(id+"F0.wireOp",EDGE,"E8.top"),sQuery(id+"F0.wireOp",EDGE,"E8.left"),sQuery(id+"F0.wireOp",EDGE,"E8.right"),sQuery(id+"F0.wireOp",EDGE,"E9.bottom"),sQuery(id+"F0.wireOp",EDGE,"E9.top"),sQuery(id+"F0.wireOp",EDGE,"E9.left"),sQuery(id+"F0.wireOp",EDGE,"E9.right"),sQuery(id+"F0.wireOp",EDGE,"E10.bottom"),sQuery(id+"F0.wireOp",EDGE,"E10.top"),sQuery(id+"F0.wireOp",EDGE,"E10.left"),sQuery(id+"F0.wireOp",EDGE,"E10.right"),sQuery(id+"F0.wireOp",EDGE,"E12"),sQuery(id+"F0.wireOp",EDGE,"E13"),sQuery(id+"F0.wireOp",EDGE,"E14"),sQuery(id+"F0.wireOp",EDGE,"E15"),sQuery(id+"F0.wireOp",EDGE,"E16"),sQuery(id+"F0.wireOp",EDGE,"E17")])],"isStart":true});
            var sketch = newSketch(context, id + "F18", { "sketchPlane" : qUnion([Q0])});
            skLineSegment(sketch, "E104.bottom", {"start": v(0, -7.8) * mm, "end": v(-12.7, -7.8) * mm});
            skLineSegment(sketch, "E104.top", {"start": v(0, -8.1) * mm, "end": v(-12.7, -8.1) * mm});
            skLineSegment(sketch, "E104.left", {"start": v(0, -7.8) * mm, "end": v(0, -8.1) * mm});
            skLineSegment(sketch, "E104.right", {"start": v(-12.7, -7.8) * mm, "end": v(-12.7, -8.1) * mm});
            skLineSegment(sketch, "E105.bottom", {"start": v(156, -7.8) * mm, "end": v(168.7, -7.8) * mm});
            skLineSegment(sketch, "E105.top", {"start": v(156, -8.1) * mm, "end": v(168.7, -8.1) * mm});
            skLineSegment(sketch, "E105.left", {"start": v(156, -7.8) * mm, "end": v(156, -8.1) * mm});
            skLineSegment(sketch, "E105.right", {"start": v(168.7, -7.8) * mm, "end": v(168.7, -8.1) * mm});
            skLineSegment(sketch, "E106", {"start": v(-682, -45.87) * mm, "end": v(-682, 89.51) * mm});
            skSolve(sketch);
        }
        {
            var Q0;
            Q0=makeQuery(id+"F18.imprint","IMPRINT",FACE,{"disambiguationData":[TD([[makeQuery(id+"F18.imprint","IMPRINT",EDGE,{"derivedFrom":sQuery(id+"F18.wireOp",EDGE,"E105.bottom")}),-1.0]])]});
            var Q1;
            Q1=makeQuery(id+"F18.imprint","IMPRINT",FACE,{"disambiguationData":[TD([[makeQuery(id+"F18.imprint","IMPRINT",EDGE,{"derivedFrom":sQuery(id+"F18.wireOp",EDGE,"E104.bottom")}),-1.0]])]});
            var Q2;
            Q2=sQuery(id+"F18.wireOp",EDGE,"E106");
            revolve(context, id + "F19", {"operationType" : NewBodyOperationType.ADD, "entities" : qUnion([Q0, Q1]), "axis" : qUnion([Q2]), "revolveType" : RevolveType.ONE_DIRECTION, "angle" : 5.62 * degree});
        }
        {
            var Q0;
            Q0=makeQuery(id+"F19.boolean.opBoolean","MERGE",FACE,{"derivedFrom":[makeQuery(id+"F1.opRevolve","CAP_FACE",FACE,{"disambiguationData":[OSD([sQuery(id+"F0.wireOp",EDGE,"E0"),sQuery(id+"F0.wireOp",EDGE,"E1"),sQuery(id+"F0.wireOp",EDGE,"E3.top"),sQuery(id+"F0.wireOp",EDGE,"E3.left"),sQuery(id+"F0.wireOp",EDGE,"E3.right"),sQuery(id+"F0.wireOp",EDGE,"E4.top"),sQuery(id+"F0.wireOp",EDGE,"E4.left"),sQuery(id+"F0.wireOp",EDGE,"E4.right"),sQuery(id+"F0.wireOp",EDGE,"E5.trimOffspring"),sQuery(id+"F0.wireOp",EDGE,"E6.trimOffspring"),sQuery(id+"F0.wireOp",EDGE,"E7.bottom"),sQuery(id+"F0.wireOp",EDGE,"E7.top"),sQuery(id+"F0.wireOp",EDGE,"E7.left"),sQuery(id+"F0.wireOp",EDGE,"E7.right"),sQuery(id+"F0.wireOp",EDGE,"E8.bottom"),sQuery(id+"F0.wireOp",EDGE,"E8.top"),sQuery(id+"F0.wireOp",EDGE,"E8.left"),sQuery(id+"F0.wireOp",EDGE,"E8.right"),sQuery(id+"F0.wireOp",EDGE,"E9.bottom"),sQuery(id+"F0.wireOp",EDGE,"E9.top"),sQuery(id+"F0.wireOp",EDGE,"E9.left"),sQuery(id+"F0.wireOp",EDGE,"E9.right"),sQuery(id+"F0.wireOp",EDGE,"E10.bottom"),sQuery(id+"F0.wireOp",EDGE,"E10.top"),sQuery(id+"F0.wireOp",EDGE,"E10.left"),sQuery(id+"F0.wireOp",EDGE,"E10.right"),sQuery(id+"F0.wireOp",EDGE,"E12"),sQuery(id+"F0.wireOp",EDGE,"E13"),sQuery(id+"F0.wireOp",EDGE,"E14"),sQuery(id+"F0.wireOp",EDGE,"E15"),sQuery(id+"F0.wireOp",EDGE,"E16"),sQuery(id+"F0.wireOp",EDGE,"E17")])],"isStart":true}),makeQuery(id+"F19.opRevolve","CAP_FACE",FACE,{"disambiguationData":[OSD([sQuery(id+"F18.wireOp",EDGE,"E104.bottom"),sQuery(id+"F18.wireOp",EDGE,"E104.top"),sQuery(id+"F18.wireOp",EDGE,"E104.left"),sQuery(id+"F18.wireOp",EDGE,"E104.right")])],"isStart":true}),makeQuery(id+"F19.opRevolve","CAP_FACE",FACE,{"disambiguationData":[OSD([sQuery(id+"F18.wireOp",EDGE,"E105.bottom"),sQuery(id+"F18.wireOp",EDGE,"E105.top"),sQuery(id+"F18.wireOp",EDGE,"E105.left"),sQuery(id+"F18.wireOp",EDGE,"E105.right")])],"isStart":true})]});
            var sketch = newSketch(context, id + "F20", { "sketchPlane" : qUnion([Q0])});
            skLineSegment(sketch, "E107.bottom", {"start": v(166.85, 0) * mm, "end": v(166.35, 0) * mm});
            skLineSegment(sketch, "E107.top", {"start": v(166.85, 10) * mm, "end": v(166.35, 10) * mm});
            skLineSegment(sketch, "E107.left", {"start": v(166.85, 0) * mm, "end": v(166.85, 10) * mm});
            skLineSegment(sketch, "E107.right", {"start": v(166.35, 0) * mm, "end": v(166.35, 10) * mm});
            skLineSegment(sketch, "E108.bottom", {"start": v(-10.23, 0) * mm, "end": v(-10.73, 0) * mm});
            skLineSegment(sketch, "E108.top", {"start": v(-10.23, 10) * mm, "end": v(-10.73, 10) * mm});
            skLineSegment(sketch, "E108.left", {"start": v(-10.23, 0) * mm, "end": v(-10.23, 10) * mm});
            skLineSegment(sketch, "E108.right", {"start": v(-10.73, 0) * mm, "end": v(-10.73, 10) * mm});
            skLineSegment(sketch, "E109", {"start": v(-682, -17.05) * mm, "end": v(-682, 58.54) * mm});
            skSolve(sketch);
        }
        {
            var Q0;
            Q0=makeQuery(id+"F20.imprint","IMPRINT",FACE,{"disambiguationData":[TD([[makeQuery(id+"F20.imprint","IMPRINT",EDGE,{"derivedFrom":sQuery(id+"F20.wireOp",EDGE,"E107.bottom")}),-1.0]])]});
            var Q1;
            Q1=makeQuery(id+"F20.imprint","IMPRINT",FACE,{"disambiguationData":[TD([[makeQuery(id+"F20.imprint","IMPRINT",EDGE,{"derivedFrom":sQuery(id+"F20.wireOp",EDGE,"E108.bottom")}),-1.0]])]});
            var Q2;
            Q2=sQuery(id+"F20.wireOp",EDGE,"E109");
            revolve(context, id + "F21", {"operationType" : NewBodyOperationType.ADD, "entities" : qUnion([Q0, Q1]), "axis" : qUnion([Q2]), "revolveType" : RevolveType.ONE_DIRECTION, "angle" : 4 * degree});
        }
        {
            var Q0;
            Q0=makeQuery(id+"F5.opExtrude","SWEPT_FACE",FACE,{"disambiguationData":[OSD([sQuery(id+"F4.wireOp",EDGE,"E68.right")])]});
            var sketch = newSketch(context, id + "F22", { "sketchPlane" : qUnion([Q0])});
            skLineSegment(sketch, "E110", {"start": v(0, 0) * mm, "end": v(-4.6, 0) * mm});
            skLineSegment(sketch, "E111", {"start": v(-4.6, 0) * mm, "end": v(0, 5.5) * mm});
            skLineSegment(sketch, "E112", {"start": v(0, 5.5) * mm, "end": v(0, 0) * mm});
            skSolve(sketch);
        }
        {
            var Q0;
            {var subQ0=sQuery(id+"F22.wireOp",EDGE,"E110");Q0=makeQuery(id+"F22.imprint","IMPRINT",FACE,{"disambiguationData":[TD([[makeQuery(id+"F22.imprint","IMPRINT",EDGE,{"derivedFrom":subQ0}),-1.0]])]});}
            extrude(context, id + "F23", {"entities" : qUnion([Q0]), "operationType" : NewBodyOperationType.REMOVE, "endBound" : BoundingType.SYMMETRIC, "oppositeDirection" : true, "depth" : 400 * mm, "offsetDistance" : 25 * mm});
        }
        {
            var Q0;
            Q0=makeQuery(id+"F21.opRevolve","SWEPT_FACE",FACE,{"disambiguationData":[OSD([sQuery(id+"F20.wireOp",EDGE,"E107.top")])]});
            var sketch = newSketch(context, id + "F24", { "sketchPlane" : qUnion([Q0])});
            skLineSegment(sketch, "E113", {"start": v(166.85, 0) * mm, "end": v(169.31, 0) * mm});
            skLineSegment(sketch, "E114", {"start": v(169.31, 0) * mm, "end": v(166.57, 2.95) * mm});
            skLineSegment(sketch, "E115", {"start": v(166.57, 2.95) * mm, "end": v(164.16, 0) * mm});
            skLineSegment(sketch, "E116", {"start": v(164.16, 0) * mm, "end": v(166.85, 0) * mm});
            skSolve(sketch);
        }
        {
            var Q0;
            {var subQ0=sQuery(id+"F24.wireOp",EDGE,"E113");Q0=makeQuery(id+"F24.imprint","IMPRINT",FACE,{"disambiguationData":[TD([[makeQuery(id+"F24.imprint","IMPRINT",EDGE,{"derivedFrom":subQ0}),1.0]])]});}
            var Q1;
            {var subQ4=sQuery(id+"F24.wireOp",EDGE,"E114");var subQ8=sQuery(id+"F24.wireOp",EDGE,"E115");var subQ9=makeQuery(id+"F24.imprint","INTERSECT",VERTEX,{"derivedFrom":[subQ4,subQ8]});Q1=makeQuery(id+"F24.imprint","IMPRINT",FACE,{"disambiguationData":[TD([[makeQuery(id+"F24.imprint","IMPRINT",EDGE,{"disambiguationData":[TD([[subQ9,1.0]])],"derivedFrom":subQ4}),1.0]])]});}
            var Q2;
            {var subQ0=sQuery(id+"F24.wireOp",EDGE,"E116");var subQ1=sQuery(id+"F24.wireOp",EDGE,"E115");var subQ2=makeQuery(id+"F24.imprint","INTERSECT",VERTEX,{"derivedFrom":[subQ1,subQ0]});Q2=makeQuery(id+"F24.imprint","IMPRINT",FACE,{"disambiguationData":[TD([[makeQuery(id+"F24.imprint","IMPRINT",EDGE,{"disambiguationData":[TD([[subQ2,1.0]])],"derivedFrom":subQ1}),1.0]])]});}
            extrude(context, id + "F25", {"entities" : qUnion([Q0, Q1, Q2]), "operationType" : NewBodyOperationType.ADD, "oppositeDirection" : true, "depth" : 7 * mm, "offsetDistance" : 25 * mm});
        }
        {
            var Q0;
            Q0=makeQuery(id+"F21.opRevolve","SWEPT_FACE",FACE,{"disambiguationData":[OSD([sQuery(id+"F20.wireOp",EDGE,"E108.top")])]});
            var sketch = newSketch(context, id + "F26", { "sketchPlane" : qUnion([Q0])});
            skLineSegment(sketch, "E117", {"start": v(-10.23, 0) * mm, "end": v(-7.67, 0) * mm});
            skLineSegment(sketch, "E118", {"start": v(-7.67, 0) * mm, "end": v(-10.5, 2.88) * mm});
            skLineSegment(sketch, "E119", {"start": v(-10.5, 2.88) * mm, "end": v(-13.02, 0) * mm});
            skLineSegment(sketch, "E120", {"start": v(-13.02, 0) * mm, "end": v(-10.23, 0) * mm});
            skSolve(sketch);
        }
        {
            var Q0;
            {var subQ0=sQuery(id+"F26.wireOp",EDGE,"E117");Q0=makeQuery(id+"F26.imprint","IMPRINT",FACE,{"disambiguationData":[TD([[makeQuery(id+"F26.imprint","IMPRINT",EDGE,{"derivedFrom":subQ0}),1.0]])]});}
            var Q1;
            {var subQ4=sQuery(id+"F26.wireOp",EDGE,"E118");var subQ8=sQuery(id+"F26.wireOp",EDGE,"E119");var subQ9=makeQuery(id+"F26.imprint","INTERSECT",VERTEX,{"derivedFrom":[subQ4,subQ8]});Q1=makeQuery(id+"F26.imprint","IMPRINT",FACE,{"disambiguationData":[TD([[makeQuery(id+"F26.imprint","IMPRINT",EDGE,{"disambiguationData":[TD([[subQ9,1.0]])],"derivedFrom":subQ4}),1.0]])]});}
            var Q2;
            {var subQ0=sQuery(id+"F26.wireOp",EDGE,"E120");var subQ1=sQuery(id+"F26.wireOp",EDGE,"E119");var subQ2=makeQuery(id+"F26.imprint","INTERSECT",VERTEX,{"derivedFrom":[subQ1,subQ0]});Q2=makeQuery(id+"F26.imprint","IMPRINT",FACE,{"disambiguationData":[TD([[makeQuery(id+"F26.imprint","IMPRINT",EDGE,{"disambiguationData":[TD([[subQ2,1.0]])],"derivedFrom":subQ1}),1.0]])]});}
            extrude(context, id + "F27", {"entities" : qUnion([Q0, Q1, Q2]), "operationType" : NewBodyOperationType.ADD, "oppositeDirection" : true, "depth" : 7 * mm, "offsetDistance" : 25 * mm});
        }
        {
            var Q0;
            Q0=makeQuery(id+"F1.opRevolve","SWEPT_BODY",BODY,{"disambiguationData":[OSD([sQuery(id+"F0.wireOp",EDGE,"E0"),sQuery(id+"F0.wireOp",EDGE,"E1"),sQuery(id+"F0.wireOp",EDGE,"E3.top"),sQuery(id+"F0.wireOp",EDGE,"E3.left"),sQuery(id+"F0.wireOp",EDGE,"E3.right"),sQuery(id+"F0.wireOp",EDGE,"E4.top"),sQuery(id+"F0.wireOp",EDGE,"E4.left"),sQuery(id+"F0.wireOp",EDGE,"E4.right"),sQuery(id+"F0.wireOp",EDGE,"E5.trimOffspring"),sQuery(id+"F0.wireOp",EDGE,"E6.trimOffspring"),sQuery(id+"F0.wireOp",EDGE,"E7.bottom"),sQuery(id+"F0.wireOp",EDGE,"E7.top"),sQuery(id+"F0.wireOp",EDGE,"E7.left"),sQuery(id+"F0.wireOp",EDGE,"E7.right"),sQuery(id+"F0.wireOp",EDGE,"E8.bottom"),sQuery(id+"F0.wireOp",EDGE,"E8.top"),sQuery(id+"F0.wireOp",EDGE,"E8.left"),sQuery(id+"F0.wireOp",EDGE,"E8.right"),sQuery(id+"F0.wireOp",EDGE,"E9.bottom"),sQuery(id+"F0.wireOp",EDGE,"E9.top"),sQuery(id+"F0.wireOp",EDGE,"E9.left"),sQuery(id+"F0.wireOp",EDGE,"E9.right"),sQuery(id+"F0.wireOp",EDGE,"E10.bottom"),sQuery(id+"F0.wireOp",EDGE,"E10.top"),sQuery(id+"F0.wireOp",EDGE,"E10.left"),sQuery(id+"F0.wireOp",EDGE,"E10.right"),sQuery(id+"F0.wireOp",EDGE,"E12"),sQuery(id+"F0.wireOp",EDGE,"E13"),sQuery(id+"F0.wireOp",EDGE,"E14"),sQuery(id+"F0.wireOp",EDGE,"E15"),sQuery(id+"F0.wireOp",EDGE,"E16"),sQuery(id+"F0.wireOp",EDGE,"E17")])]});
            var Q1;
            Q1=makeQuery(id+"F25.boolean.opBoolean","MERGE",FACE,{"derivedFrom":[makeQuery(id+"F21.opRevolve","SWEPT_FACE",FACE,{"disambiguationData":[OSD([sQuery(id+"F20.wireOp",EDGE,"E107.top")])]}),makeQuery(id+"F25.opExtrude","CAP_FACE",FACE,{"disambiguationData":[OSD([sQuery(id+"F24.wireOp",EDGE,"E113"),sQuery(id+"F24.wireOp",EDGE,"E114"),sQuery(id+"F24.wireOp",EDGE,"E115"),sQuery(id+"F24.wireOp",EDGE,"E116")])],"isStart":true})]});
            mirror(context, id + "F28", {"operationType" : NewBodyOperationType.ADD, "entities" : qUnion([Q0]), "mirrorPlane" : qUnion([Q1])});
        }
    });
